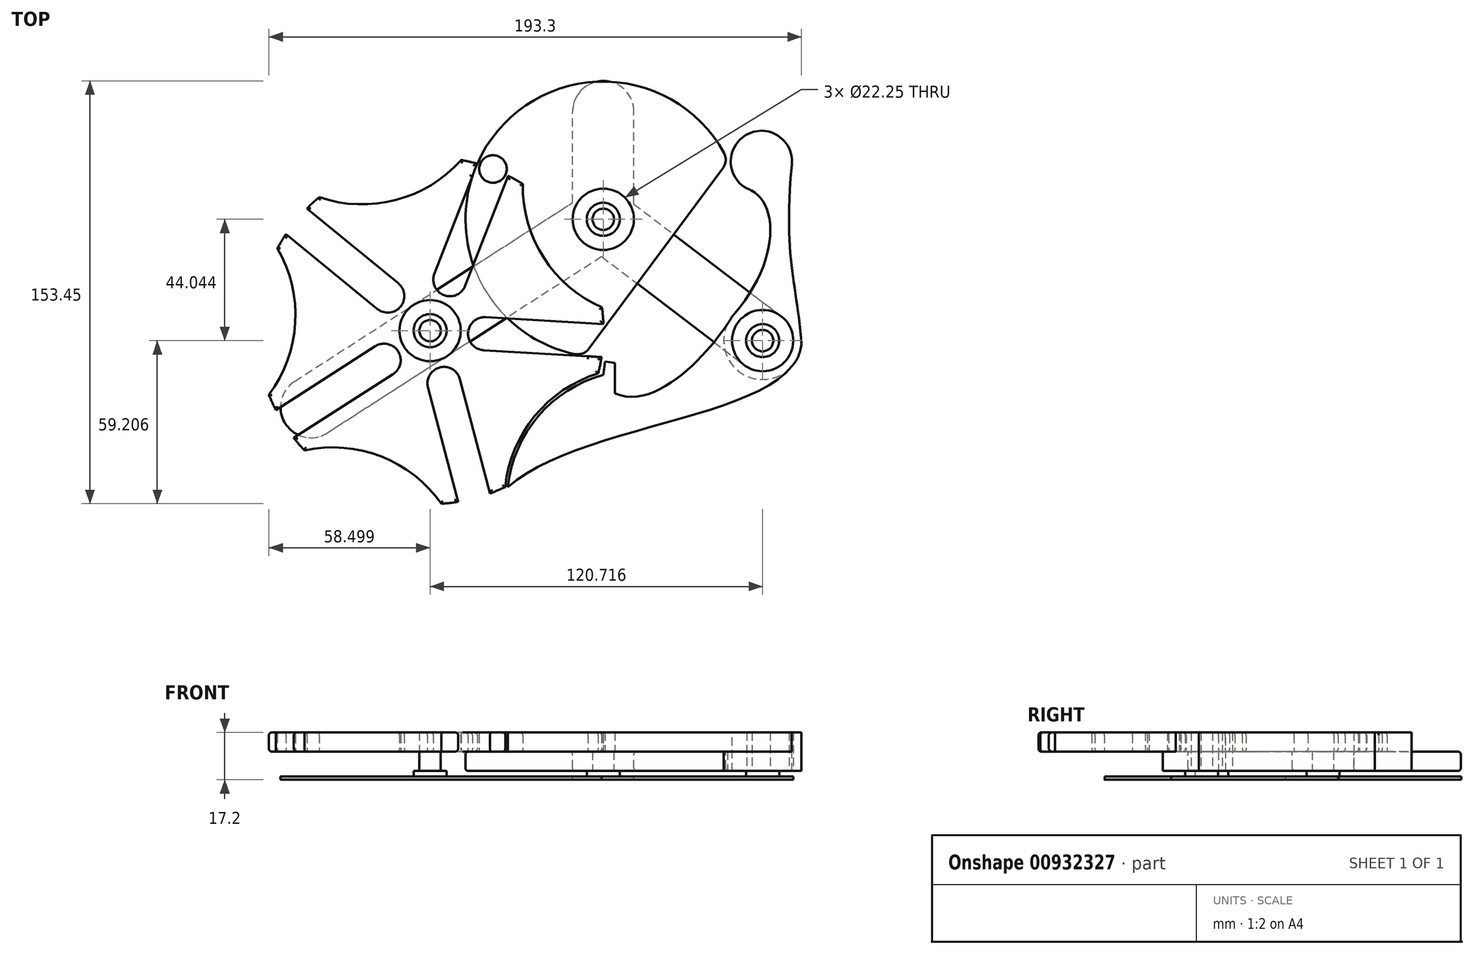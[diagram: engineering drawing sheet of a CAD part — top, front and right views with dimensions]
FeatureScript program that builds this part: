
annotation { "Feature Type Name" : "Feature", "Feature Type Description" : "" }
export const myFeature = defineFeature(function(context is Context, id is Id, definition is map)
    precondition{}
    {
        {
            assignVariable(context, id + "F0", {"name" : "BHeight", "anyValue" : 7});
        }
        {
            var Q0;
            Q0=qCreatedBy(makeId("Top.planeOp"),FACE);
            var sketch = newSketch(context, id + "F1", { "sketchPlane" : qUnion([Q0])});
            skCircle(sketch, "E0", {"center": v(0, 0) * mm, "radius": 11.12 * mm});
            skCircle(sketch, "E1", {"center": v(0, 0) * mm, "radius": 50 * mm});
            skCircle(sketch, "E2", {"center": v(-40.03, 18.26) * mm, "radius": 5 * mm});
            skLineSegment(sketch, "E3", {"start": v(0, 0) * mm, "end": v(-45.5, 20.75) * mm, "construction": true});
            skArc(sketch, "E4", {"start": v(-115.19, -5.4) * mm, "mid": v(-116.8, -7.94) * mm, "end": v(-118.28, -10.55) * mm});
            skLineSegment(sketch, "E5", {"start": v(-40.03, 18.26) * mm, "end": v(-62.86, -40.42) * mm, "construction": true});
            skLineSegment(sketch, "E6", {"start": v(-62.86, -40.42) * mm, "end": v(0, -44) * mm, "construction": true});
            skLineSegment(sketch, "E7", {"start": v(0, 0) * mm, "end": v(0, -44) * mm, "construction": true});
            skLineSegment(sketch, "E8", {"start": v(-34.55, 15.81) * mm, "end": v(-50.08, -24.13) * mm});
            skLineSegment(sketch, "E9", {"start": v(-45.73, 20.16) * mm, "end": v(-61.27, -19.78) * mm});
            skArc(sketch, "E10", {"start": v(-61.27, -19.78) * mm, "mid": v(-57.85, -27.55) * mm, "end": v(-50.08, -24.13) * mm});
            skLineSegment(sketch, "E11.1.0", {"start": v(-115.19, -5.4) * mm, "end": v(-82, -32.53) * mm});
            skLineSegment(sketch, "E11.1.1", {"start": v(-107.6, 3.88) * mm, "end": v(-74.4, -23.24) * mm});
            skArc(sketch, "E11.1.2", {"start": v(-82, -32.53) * mm, "mid": v(-73.56, -31.68) * mm, "end": v(-74.4, -23.24) * mm});
            skLineSegment(sketch, "E11.2.0", {"start": v(-112.33, -79.37) * mm, "end": v(-76.28, -56.19) * mm});
            skLineSegment(sketch, "E11.2.1", {"start": v(-118.82, -69.28) * mm, "end": v(-82.77, -46.1) * mm});
            skArc(sketch, "E11.2.2", {"start": v(-76.28, -56.19) * mm, "mid": v(-74.48, -47.9) * mm, "end": v(-82.77, -46.1) * mm});
            skLineSegment(sketch, "E11.3.0", {"start": v(-41.1, -99.5) * mm, "end": v(-52.02, -58.06) * mm});
            skLineSegment(sketch, "E11.3.1", {"start": v(-52.71, -102.56) * mm, "end": v(-63.62, -61.12) * mm});
            skArc(sketch, "E11.3.2", {"start": v(-52.02, -58.06) * mm, "mid": v(-59.34, -53.79) * mm, "end": v(-63.62, -61.12) * mm});
            skLineSegment(sketch, "E11.4.0", {"start": v(0.05, -38) * mm, "end": v(-42.73, -35.56) * mm});
            skLineSegment(sketch, "E11.4.1", {"start": v(-0.63, -49.97) * mm, "end": v(-43.42, -47.54) * mm});
            skArc(sketch, "E11.4.2", {"start": v(-42.73, -35.56) * mm, "mid": v(-49.07, -41.2) * mm, "end": v(-43.42, -47.54) * mm});
            skCircle(sketch, "E12", {"center": v(-62.86, -40.42) * mm, "radius": 11.12 * mm});
            skArc(sketch, "E13.trimOffspring", {"start": v(-112.33, -79.37) * mm, "mid": v(-110.42, -81.68) * mm, "end": v(-108.4, -83.9) * mm});
            skArc(sketch, "E14.trimOffspring", {"start": v(-41.1, -99.5) * mm, "mid": v(-38.32, -98.4) * mm, "end": v(-35.58, -97.17) * mm});
            skArc(sketch, "E15.trimOffspring", {"start": v(0.05, -38) * mm, "mid": v(-0.13, -35) * mm, "end": v(-0.46, -32.02) * mm});
            skArc(sketch, "E16.trimOffspring", {"start": v(-45.73, 20.16) * mm, "mid": v(-48.64, 20.91) * mm, "end": v(-51.57, 21.52) * mm});
            skArc(sketch, "E17", {"start": v(-1.85, -55.97) * mm, "mid": v(-24.93, -71.48) * mm, "end": v(-35.58, -97.17) * mm});
            skArc(sketch, "E18.trimOffspring", {"start": v(-1.85, -55.97) * mm, "mid": v(-1.16, -52.99) * mm, "end": v(-0.63, -49.97) * mm});
            skArc(sketch, "E19.1.0", {"start": v(-29.22, 12.8) * mm, "mid": v(-21.6, -13.95) * mm, "end": v(-0.46, -32.02) * mm});
            skArc(sketch, "E19.2.0", {"start": v(-103.08, 8.02) * mm, "mid": v(-75.29, 7) * mm, "end": v(-51.57, 21.52) * mm});
            skArc(sketch, "E19.3.0", {"start": v(-121.36, -63.7) * mm, "mid": v(-111.8, -37.6) * mm, "end": v(-118.28, -10.55) * mm});
            skArc(sketch, "E19.4.0", {"start": v(-58.8, -103.25) * mm, "mid": v(-80.68, -86.1) * mm, "end": v(-108.4, -83.9) * mm});
            skCircle(sketch, "E20", {"center": v(57.86, -44.04) * mm, "radius": 11.12 * mm});
            skArc(sketch, "E21.0", {"start": v(0, -56.48) * mm, "mid": v(-23.64, -71.5) * mm, "end": v(-34.59, -97.27) * mm});
            skLineSegment(sketch, "E22", {"start": v(0.7, -51.66) * mm, "end": v(0, -56.48) * mm});
            skLineSegment(sketch, "E23", {"start": v(0.7, -51.66) * mm, "end": v(4.2, -52.16) * mm});
            skLineSegment(sketch, "E24", {"start": v(4.2, -52.16) * mm, "end": v(4.2, -63.16) * mm});
            skCircle(sketch, "E25", {"center": v(57.86, -44.04) * mm, "radius": 14.12 * mm});
            skFitSpline(sketch, "E26", {"points": [v(4.2, -63.16) * mm, v(46.79, -35.27) * mm], "startDerivative": vector(48.84, -21.94) * mm, "endDerivative": vector(16.55, 28.74) * mm});
            skFitSpline(sketch, "E27", {"points": [v(-34.59, -97.27) * mm, v(68.4, -53.43) * mm], "startDerivative": vector(68.8, 63.46) * mm, "endDerivative": vector(45.76, 58.07) * mm});
            skCircle(sketch, "E28", {"center": v(57.4, 21) * mm, "radius": 11.12 * mm});
            skLineSegment(sketch, "E29", {"start": v(28.74, 67) * mm, "end": v(58.91, -15.5) * mm, "construction": true});
            skLineSegment(sketch, "E30", {"start": v(57.4, 21) * mm, "end": v(0, 0) * mm, "construction": true});
            skFitSpline(sketch, "E31", {"points": [v(46.79, -35.27) * mm, v(52.14, 11.2) * mm], "startDerivative": vector(52.8, 59.6) * mm, "endDerivative": vector(-35.98, 12.72) * mm});
            skFitSpline(sketch, "E32", {"points": [v(68.3, 18.76) * mm, v(71.94, -45.11) * mm], "startDerivative": vector(-8.34, -102.87) * mm, "endDerivative": vector(5.33, -69.33) * mm});
            skLineSegment(sketch, "E33", {"start": v(45.32, 21.13) * mm, "end": v(-7.1, -49.5) * mm});
            skLineSegment(sketch, "E34", {"start": v(0, 0) * mm, "end": v(45.32, 21.13) * mm, "construction": true});
            skLineSegment(sketch, "E35", {"start": v(0, 0) * mm, "end": v(-7.1, -49.5) * mm, "construction": true});
            skLineSegment(sketch, "E36", {"start": v(3.77, -49.86) * mm, "end": v(-43.8, 24.11) * mm, "construction": true});
            skArc(sketch, "E37.trimOffspring", {"start": v(-58.8, -103.25) * mm, "mid": v(-55.75, -102.98) * mm, "end": v(-52.71, -102.56) * mm});
            skArc(sketch, "E38.trimOffspring", {"start": v(-121.36, -63.7) * mm, "mid": v(-120.16, -66.52) * mm, "end": v(-118.82, -69.28) * mm});
            skArc(sketch, "E39.trimOffspring", {"start": v(-103.08, 8.02) * mm, "mid": v(-105.39, 6) * mm, "end": v(-107.6, 3.88) * mm});
            skArc(sketch, "E40.trimOffspring", {"start": v(-29.22, 12.8) * mm, "mid": v(-31.85, 14.37) * mm, "end": v(-34.55, 15.81) * mm});
            skSolve(sketch);
        }
        {
            var Q0;
            {var subQ5=sQuery(id+"F1.wireOp",EDGE,"E15.trimOffspring");Q0=makeQuery(id+"F1.imprint","IMPRINT",FACE,{"disambiguationData":[TD([[makeQuery(id+"F1.imprint","IMPRINT",EDGE,{"derivedFrom":subQ5}),1.0]])]});}
            var Q1;
            {var subQ18=sQuery(id+"F1.wireOp",EDGE,"E10");Q1=makeQuery(id+"F1.imprint","IMPRINT",FACE,{"disambiguationData":[TD([[makeQuery(id+"F1.imprint","IMPRINT",EDGE,{"derivedFrom":subQ18}),-1.0]])]});}
            extrude(context, id + "F2", {"entities" : qUnion([Q0, Q1]), "depth" : (getVariable(context, 'BHeight')) * mm, "offsetDistance" : 25 * mm});
        }
        {
            var Q0;
            Q0=makeQuery(id+"F1.imprint","IMPRINT",FACE,{"disambiguationData":[TD([[makeQuery(id+"F1.imprint","IMPRINT",EDGE,{"derivedFrom":sQuery(id+"F1.wireOp",EDGE,"E0")}),-1.0]])]});
            var Q1;
            {var subQ5=sQuery(id+"F1.wireOp",EDGE,"E15.trimOffspring");Q1=makeQuery(id+"F1.imprint","IMPRINT",FACE,{"disambiguationData":[TD([[makeQuery(id+"F1.imprint","IMPRINT",EDGE,{"derivedFrom":subQ5}),1.0]])]});}
            var Q2;
            Q2=makeQuery(id+"F1.imprint","IMPRINT",FACE,{"disambiguationData":[TD([[makeQuery(id+"F1.imprint","IMPRINT",EDGE,{"derivedFrom":sQuery(id+"F1.wireOp",EDGE,"E2")}),1.0]])]});
            var Q3;
            {var subQ0=sQuery(id+"F1.wireOp",EDGE,"E19.1.0");Q3=makeQuery(id+"F1.imprint","IMPRINT",FACE,{"disambiguationData":[TD([[makeQuery(id+"F1.imprint","IMPRINT",EDGE,{"derivedFrom":subQ0}),1.0]])]});}
            var Q4;
            {var subQ0=sQuery(id+"F1.wireOp",EDGE,"E16.trimOffspring");var subQ1=sQuery(id+"F1.wireOp",EDGE,"E1");var subQ2=makeQuery(id+"F1.imprint","INTERSECT",VERTEX,{"derivedFrom":[subQ1,subQ0]});Q4=makeQuery(id+"F1.imprint","IMPRINT",FACE,{"disambiguationData":[TD([[makeQuery(id+"F1.imprint","IMPRINT",EDGE,{"disambiguationData":[TD([[subQ2,-1.0]])],"derivedFrom":subQ1}),1.0]])]});}
            extrude(context, id + "F3", {"entities" : qUnion([Q0, Q1, Q2, Q3, Q4]), "oppositeDirection" : true, "depth" : (getVariable(context, 'BHeight')) * mm, "offsetDistance" : 25 * mm});
        }
        {
            var Q0;
            Q0=makeQuery(id+"F1.imprint","IMPRINT",FACE,{"disambiguationData":[TD([[makeQuery(id+"F1.imprint","IMPRINT",EDGE,{"derivedFrom":sQuery(id+"F1.wireOp",EDGE,"E2")}),1.0]])]});
            var Q1;
            Q1=makeQuery(id+"F2.opExtrude","CAP_FACE",FACE,{"disambiguationData":[OSD([sQuery(id+"F1.wireOp",EDGE,"E1"),sQuery(id+"F1.wireOp",EDGE,"E4"),sQuery(id+"F1.wireOp",EDGE,"E8"),sQuery(id+"F1.wireOp",EDGE,"E9"),sQuery(id+"F1.wireOp",EDGE,"E10"),sQuery(id+"F1.wireOp",EDGE,"E11.1.0"),sQuery(id+"F1.wireOp",EDGE,"E11.1.1"),sQuery(id+"F1.wireOp",EDGE,"E11.1.2"),sQuery(id+"F1.wireOp",EDGE,"E11.2.0"),sQuery(id+"F1.wireOp",EDGE,"E11.2.1"),sQuery(id+"F1.wireOp",EDGE,"E11.2.2"),sQuery(id+"F1.wireOp",EDGE,"E11.3.0"),sQuery(id+"F1.wireOp",EDGE,"E11.3.1"),sQuery(id+"F1.wireOp",EDGE,"E11.3.2"),sQuery(id+"F1.wireOp",EDGE,"E11.4.0"),sQuery(id+"F1.wireOp",EDGE,"E11.4.1"),sQuery(id+"F1.wireOp",EDGE,"E11.4.2"),sQuery(id+"F1.wireOp",EDGE,"E12"),sQuery(id+"F1.wireOp",EDGE,"E13.trimOffspring"),sQuery(id+"F1.wireOp",EDGE,"E14.trimOffspring"),sQuery(id+"F1.wireOp",EDGE,"E15.trimOffspring"),sQuery(id+"F1.wireOp",EDGE,"E16.trimOffspring")])],"isStart":false});
            extrude(context, id + "F4", {"entities" : qUnion([Q0]), "operationType" : NewBodyOperationType.ADD, "endBound" : BoundingType.UP_TO_SURFACE, "depth" : 25 * mm, "endBoundEntityFace" : qUnion([Q1]), "offsetDistance" : 25 * mm});
        }
        {
            var Q0;
            Q0=makeQuery(id+"F3.opExtrude","CAP_FACE",FACE,{"disambiguationData":[OSD([sQuery(id+"F1.wireOp",EDGE,"E0"),sQuery(id+"F1.wireOp",EDGE,"E1"),sQuery(id+"F1.wireOp",EDGE,"E9"),sQuery(id+"F1.wireOp",EDGE,"E11.4.1"),sQuery(id+"F1.wireOp",EDGE,"E14.trimOffspring"),sQuery(id+"F1.wireOp",EDGE,"E16.trimOffspring")])],"isStart":false});
            cPlane(context, id + "F5", {"entities" : qUnion([Q0]), "cplaneType" : CPlaneType.OFFSET, "offset" : 2 * mm, "width" : 150 * mm, "height" : 150 * mm});
        }
        {
            var Q0;
            Q0=makeQuery(id+"F1.imprint","IMPRINT",FACE,{"disambiguationData":[TD([[makeQuery(id+"F1.imprint","IMPRINT",EDGE,{"derivedFrom":sQuery(id+"F1.wireOp",EDGE,"E21.0")}),1.0]])]});
            var Q1;
            Q1=makeQuery(id+"F1.imprint","IMPRINT",FACE,{"disambiguationData":[TD([[makeQuery(id+"F1.imprint","IMPRINT",EDGE,{"derivedFrom":sQuery(id+"F1.wireOp",EDGE,"E20")}),-1.0]])]});
            var Q2;
            Q2=makeQuery(id+"F2.opExtrude","CAP_FACE",FACE,{"disambiguationData":[OSD([sQuery(id+"F1.wireOp",EDGE,"E1"),sQuery(id+"F1.wireOp",EDGE,"E4"),sQuery(id+"F1.wireOp",EDGE,"E8"),sQuery(id+"F1.wireOp",EDGE,"E9"),sQuery(id+"F1.wireOp",EDGE,"E10"),sQuery(id+"F1.wireOp",EDGE,"E11.1.0"),sQuery(id+"F1.wireOp",EDGE,"E11.1.1"),sQuery(id+"F1.wireOp",EDGE,"E11.1.2"),sQuery(id+"F1.wireOp",EDGE,"E11.2.0"),sQuery(id+"F1.wireOp",EDGE,"E11.2.1"),sQuery(id+"F1.wireOp",EDGE,"E11.2.2"),sQuery(id+"F1.wireOp",EDGE,"E11.3.0"),sQuery(id+"F1.wireOp",EDGE,"E11.3.1"),sQuery(id+"F1.wireOp",EDGE,"E11.3.2"),sQuery(id+"F1.wireOp",EDGE,"E11.4.0"),sQuery(id+"F1.wireOp",EDGE,"E11.4.1"),sQuery(id+"F1.wireOp",EDGE,"E11.4.2"),sQuery(id+"F1.wireOp",EDGE,"E12"),sQuery(id+"F1.wireOp",EDGE,"E13.trimOffspring"),sQuery(id+"F1.wireOp",EDGE,"E14.trimOffspring"),sQuery(id+"F1.wireOp",EDGE,"E15.trimOffspring"),sQuery(id+"F1.wireOp",EDGE,"E16.trimOffspring"),sQuery(id+"F1.wireOp",EDGE,"E17"),sQuery(id+"F1.wireOp",EDGE,"E18.trimOffspring"),sQuery(id+"F1.wireOp",EDGE,"E19.1.0"),sQuery(id+"F1.wireOp",EDGE,"E19.2.0"),sQuery(id+"F1.wireOp",EDGE,"E19.3.0"),sQuery(id+"F1.wireOp",EDGE,"E19.4.0")])],"isStart":false});
            extrude(context, id + "F6", {"entities" : qUnion([Q0, Q1]), "endBound" : BoundingType.UP_TO_SURFACE, "depth" : 25 * mm, "endBoundEntityFace" : qUnion([Q2]), "offsetDistance" : 25 * mm});
        }
        {
            var Q0;
            Q0=makeQuery(id+"F1.imprint","IMPRINT",FACE,{"disambiguationData":[TD([[makeQuery(id+"F1.imprint","IMPRINT",EDGE,{"derivedFrom":sQuery(id+"F1.wireOp",EDGE,"E20")}),-1.0]])]});
            var Q1;
            {var subQ0=sQuery(id+"F1.wireOp",EDGE,"E31");var subQ1=sQuery(id+"F1.wireOp",EDGE,"E25");var subQ2=makeQuery(id+"F1.imprint","INTERSECT",VERTEX,{"derivedFrom":[subQ1,subQ0]});Q1=makeQuery(id+"F1.imprint","IMPRINT",FACE,{"disambiguationData":[TD([[makeQuery(id+"F1.imprint","IMPRINT",EDGE,{"disambiguationData":[TD([[subQ2,1.0]])],"derivedFrom":subQ1}),-1.0]])]});}
            var Q2;
            {var subQ0=sQuery(id+"F1.wireOp",EDGE,"E31");var subQ1=sQuery(id+"F1.wireOp",EDGE,"E28");var subQ2=makeQuery(id+"F1.imprint","INTERSECT",VERTEX,{"disambiguationData":[OD(0.0)],"derivedFrom":[subQ1,subQ0]});Q2=makeQuery(id+"F1.imprint","IMPRINT",FACE,{"disambiguationData":[TD([[makeQuery(id+"F1.imprint","IMPRINT",EDGE,{"disambiguationData":[TD([[subQ2,1.0]])],"derivedFrom":subQ1}),1.0]])]});}
            var Q3;
            Q3=makeQuery(id+"F3.opExtrude","CAP_FACE",FACE,{"disambiguationData":[OSD([sQuery(id+"F1.wireOp",EDGE,"E0"),sQuery(id+"F1.wireOp",EDGE,"E1"),sQuery(id+"F1.wireOp",EDGE,"E9"),sQuery(id+"F1.wireOp",EDGE,"E11.4.1"),sQuery(id+"F1.wireOp",EDGE,"E16.trimOffspring"),sQuery(id+"F1.wireOp",EDGE,"E18.trimOffspring")])],"isStart":false});
            extrude(context, id + "F7", {"entities" : qUnion([Q0, Q1, Q2]), "operationType" : NewBodyOperationType.ADD, "endBound" : BoundingType.UP_TO_SURFACE, "oppositeDirection" : true, "depth" : 7 * mm, "endBoundEntityFace" : qUnion([Q3]), "offsetDistance" : 25 * mm});
        }
        {
            var Q0;
            Q0=makeQuery(id+"F7.opExtrude","CAP_FACE",FACE,{"disambiguationData":[OSD([sQuery(id+"F1.wireOp",EDGE,"E20"),sQuery(id+"F1.wireOp",EDGE,"E25"),sQuery(id+"F1.wireOp",EDGE,"E26"),sQuery(id+"F1.wireOp",EDGE,"E28"),sQuery(id+"F1.wireOp",EDGE,"E31"),sQuery(id+"F1.wireOp",EDGE,"E32")])],"isStart":true});
            var Q1;
            Q1=makeQuery(id+"F6.opExtrude","CAP_FACE",FACE,{"disambiguationData":[OSD([sQuery(id+"F1.wireOp",EDGE,"E20"),sQuery(id+"F1.wireOp",EDGE,"E21.0"),sQuery(id+"F1.wireOp",EDGE,"E22"),sQuery(id+"F1.wireOp",EDGE,"E23"),sQuery(id+"F1.wireOp",EDGE,"E24"),sQuery(id+"F1.wireOp",EDGE,"E25"),sQuery(id+"F1.wireOp",EDGE,"E26"),sQuery(id+"F1.wireOp",EDGE,"E27"),sQuery(id+"F1.wireOp",EDGE,"E31"),sQuery(id+"F1.wireOp",EDGE,"E32")])],"isStart":false});
            extrude(context, id + "F8", {"entities" : qUnion([Q0]), "operationType" : NewBodyOperationType.ADD, "endBound" : BoundingType.UP_TO_SURFACE, "depth" : 25 * mm, "endBoundEntityFace" : qUnion([Q1]), "offsetDistance" : 25 * mm});
        }
        {
            var Q0;
            Q0=qCreatedBy(id+"F5.planeOp",FACE);
            var sketch = newSketch(context, id + "F9", { "sketchPlane" : qUnion([Q0])});
            skCircle(sketch, "E41.0", {"center": v(0, 0) * mm, "radius": 11.12 * mm});
            skCircle(sketch, "E42.0", {"center": v(-62.86, 40.42) * mm, "radius": 11.12 * mm});
            skLineSegment(sketch, "E43", {"start": v(-68.88, 31.07) * mm, "end": v(-6.02, -9.36) * mm});
            skLineSegment(sketch, "E44", {"start": v(6.02, 9.36) * mm, "end": v(-56.84, 49.78) * mm});
            skCircle(sketch, "E45.0", {"center": v(57.86, 44.04) * mm, "radius": 11.12 * mm});
            skLineSegment(sketch, "E46", {"start": v(6.74, -8.85) * mm, "end": v(64.6, 35.2) * mm});
            skLineSegment(sketch, "E47", {"start": v(-6.74, 8.85) * mm, "end": v(51.12, 52.9) * mm});
            skCircle(sketch, "E48", {"center": v(57.86, 44.04) * mm, "radius": 6 * mm});
            skCircle(sketch, "E49", {"center": v(0, 0) * mm, "radius": 6 * mm});
            skCircle(sketch, "E50", {"center": v(-62.86, 40.42) * mm, "radius": 6 * mm});
            skCircle(sketch, "E51", {"center": v(-62.86, 40.42) * mm, "radius": 3.88 * mm});
            skCircle(sketch, "E52", {"center": v(0, 0) * mm, "radius": 3.88 * mm});
            skCircle(sketch, "E53", {"center": v(57.86, 44.04) * mm, "radius": 3.88 * mm});
            skCircle(sketch, "E54", {"center": v(-106.03, 68.18) * mm, "radius": 11.12 * mm});
            skCircle(sketch, "E55", {"center": v(0, -39.08) * mm, "radius": 11.12 * mm});
            skLineSegment(sketch, "E56", {"start": v(-112.04, 58.82) * mm, "end": v(-68.88, 31.07) * mm});
            skLineSegment(sketch, "E57", {"start": v(-56.84, 49.78) * mm, "end": v(-100.01, 77.54) * mm});
            skLineSegment(sketch, "E58", {"start": v(-11.12, 0) * mm, "end": v(-11.12, -39.08) * mm});
            skLineSegment(sketch, "E59", {"start": v(11.12, 0) * mm, "end": v(11.13, -39.08) * mm});
            skSolve(sketch);
        }
        {
            var Q0;
            Q0 = qSketchRegion(id + "F9", true);
            var Q1;
            Q1=makeQuery(id+"F9.imprint","IMPRINT",FACE,{"disambiguationData":[TD([[makeQuery(id+"F9.imprint","IMPRINT",EDGE,{"derivedFrom":sQuery(id+"F9.wireOp",EDGE,"E48")}),1.0]])]});
            var Q2;
            Q2=makeQuery(id+"F9.imprint","IMPRINT",FACE,{"disambiguationData":[TD([[makeQuery(id+"F9.imprint","IMPRINT",EDGE,{"derivedFrom":sQuery(id+"F9.wireOp",EDGE,"E53")}),1.0]])]});
            var Q3;
            Q3=makeQuery(id+"F9.imprint","IMPRINT",FACE,{"disambiguationData":[TD([[makeQuery(id+"F9.imprint","IMPRINT",EDGE,{"derivedFrom":sQuery(id+"F9.wireOp",EDGE,"E49")}),1.0]])]});
            var Q4;
            Q4=makeQuery(id+"F9.imprint","IMPRINT",FACE,{"disambiguationData":[TD([[makeQuery(id+"F9.imprint","IMPRINT",EDGE,{"derivedFrom":sQuery(id+"F9.wireOp",EDGE,"E52")}),1.0]])]});
            var Q5;
            Q5=makeQuery(id+"F9.imprint","IMPRINT",FACE,{"disambiguationData":[TD([[makeQuery(id+"F9.imprint","IMPRINT",EDGE,{"derivedFrom":sQuery(id+"F9.wireOp",EDGE,"E50")}),1.0]])]});
            var Q6;
            Q6=makeQuery(id+"F9.imprint","IMPRINT",FACE,{"disambiguationData":[TD([[makeQuery(id+"F9.imprint","IMPRINT",EDGE,{"derivedFrom":sQuery(id+"F9.wireOp",EDGE,"E51")}),1.0]])]});
            var Q7;
            Q7=makeQuery(id+"F9.imprint","IMPRINT",FACE,{"disambiguationData":[TD([[makeQuery(id+"F9.imprint","IMPRINT",EDGE,{"derivedFrom":sQuery(id+"F9.wireOp",EDGE,"E49")}),-1.0]])]});
            extrude(context, id + "F10", {"entities" : qUnion([Q0, Q1, Q2, Q3, Q4, Q5, Q6, Q7]), "depth" : 1.2 * mm, "offsetDistance" : 25 * mm});
        }
        {
            var Q0;
            Q0=makeQuery(id+"F2.opExtrude","CAP_FACE",FACE,{"disambiguationData":[OSD([sQuery(id+"F1.wireOp",EDGE,"E1"),sQuery(id+"F1.wireOp",EDGE,"E4"),sQuery(id+"F1.wireOp",EDGE,"E8"),sQuery(id+"F1.wireOp",EDGE,"E9"),sQuery(id+"F1.wireOp",EDGE,"E10"),sQuery(id+"F1.wireOp",EDGE,"E11.1.0"),sQuery(id+"F1.wireOp",EDGE,"E11.1.1"),sQuery(id+"F1.wireOp",EDGE,"E11.1.2"),sQuery(id+"F1.wireOp",EDGE,"E11.2.0"),sQuery(id+"F1.wireOp",EDGE,"E11.2.1"),sQuery(id+"F1.wireOp",EDGE,"E11.2.2"),sQuery(id+"F1.wireOp",EDGE,"E11.3.0"),sQuery(id+"F1.wireOp",EDGE,"E11.3.1"),sQuery(id+"F1.wireOp",EDGE,"E11.3.2"),sQuery(id+"F1.wireOp",EDGE,"E11.4.0"),sQuery(id+"F1.wireOp",EDGE,"E11.4.1"),sQuery(id+"F1.wireOp",EDGE,"E11.4.2"),sQuery(id+"F1.wireOp",EDGE,"E12"),sQuery(id+"F1.wireOp",EDGE,"E13.trimOffspring"),sQuery(id+"F1.wireOp",EDGE,"E14.trimOffspring"),sQuery(id+"F1.wireOp",EDGE,"E15.trimOffspring"),sQuery(id+"F1.wireOp",EDGE,"E16.trimOffspring"),sQuery(id+"F1.wireOp",EDGE,"E17"),sQuery(id+"F1.wireOp",EDGE,"E18.trimOffspring"),sQuery(id+"F1.wireOp",EDGE,"E19.1.0"),sQuery(id+"F1.wireOp",EDGE,"E19.2.0"),sQuery(id+"F1.wireOp",EDGE,"E19.3.0"),sQuery(id+"F1.wireOp",EDGE,"E19.4.0")])],"isStart":false});
            var Q1;
            Q1=makeQuery(id+"F2.opExtrude","CAP_FACE",FACE,{"disambiguationData":[OSD([sQuery(id+"F1.wireOp",EDGE,"E1"),sQuery(id+"F1.wireOp",EDGE,"E4"),sQuery(id+"F1.wireOp",EDGE,"E8"),sQuery(id+"F1.wireOp",EDGE,"E9"),sQuery(id+"F1.wireOp",EDGE,"E10"),sQuery(id+"F1.wireOp",EDGE,"E11.1.0"),sQuery(id+"F1.wireOp",EDGE,"E11.1.1"),sQuery(id+"F1.wireOp",EDGE,"E11.1.2"),sQuery(id+"F1.wireOp",EDGE,"E11.2.0"),sQuery(id+"F1.wireOp",EDGE,"E11.2.1"),sQuery(id+"F1.wireOp",EDGE,"E11.2.2"),sQuery(id+"F1.wireOp",EDGE,"E11.3.0"),sQuery(id+"F1.wireOp",EDGE,"E11.3.1"),sQuery(id+"F1.wireOp",EDGE,"E11.3.2"),sQuery(id+"F1.wireOp",EDGE,"E11.4.0"),sQuery(id+"F1.wireOp",EDGE,"E11.4.1"),sQuery(id+"F1.wireOp",EDGE,"E11.4.2"),sQuery(id+"F1.wireOp",EDGE,"E12"),sQuery(id+"F1.wireOp",EDGE,"E13.trimOffspring"),sQuery(id+"F1.wireOp",EDGE,"E14.trimOffspring"),sQuery(id+"F1.wireOp",EDGE,"E15.trimOffspring"),sQuery(id+"F1.wireOp",EDGE,"E16.trimOffspring"),sQuery(id+"F1.wireOp",EDGE,"E17"),sQuery(id+"F1.wireOp",EDGE,"E18.trimOffspring"),sQuery(id+"F1.wireOp",EDGE,"E19.1.0"),sQuery(id+"F1.wireOp",EDGE,"E19.2.0"),sQuery(id+"F1.wireOp",EDGE,"E19.3.0"),sQuery(id+"F1.wireOp",EDGE,"E19.4.0")])],"isStart":true});
            var Q2;
            Q2=makeQuery(id+"F6.opExtrude","CAP_FACE",FACE,{"disambiguationData":[OSD([sQuery(id+"F1.wireOp",EDGE,"E20"),sQuery(id+"F1.wireOp",EDGE,"E21.0"),sQuery(id+"F1.wireOp",EDGE,"E22"),sQuery(id+"F1.wireOp",EDGE,"E23"),sQuery(id+"F1.wireOp",EDGE,"E24"),sQuery(id+"F1.wireOp",EDGE,"E25"),sQuery(id+"F1.wireOp",EDGE,"E26"),sQuery(id+"F1.wireOp",EDGE,"E27"),sQuery(id+"F1.wireOp",EDGE,"E31"),sQuery(id+"F1.wireOp",EDGE,"E32")])],"isStart":false});
            var Q3;
            Q3=makeQuery(id+"F4.opExtrude","CAP_FACE",FACE,{"disambiguationData":[OSD([sQuery(id+"F1.wireOp",EDGE,"E2")])],"isStart":false});
            var Q4;
            Q4=makeQuery(id+"F7.opExtrude","CAP_FACE",FACE,{"disambiguationData":[OSD([sQuery(id+"F1.wireOp",EDGE,"E20"),sQuery(id+"F1.wireOp",EDGE,"E25"),sQuery(id+"F1.wireOp",EDGE,"E26"),sQuery(id+"F1.wireOp",EDGE,"E28"),sQuery(id+"F1.wireOp",EDGE,"E31"),sQuery(id+"F1.wireOp",EDGE,"E32")])],"isStart":true});
            var Q5;
            Q5=makeQuery(id+"F7.opExtrude","CAP_FACE",FACE,{"disambiguationData":[OSD([sQuery(id+"F1.wireOp",EDGE,"E20"),sQuery(id+"F1.wireOp",EDGE,"E25"),sQuery(id+"F1.wireOp",EDGE,"E26"),sQuery(id+"F1.wireOp",EDGE,"E28"),sQuery(id+"F1.wireOp",EDGE,"E31"),sQuery(id+"F1.wireOp",EDGE,"E32")])],"isStart":false});
            var Q6;
            Q6=makeQuery(id+"F6.opExtrude","CAP_FACE",FACE,{"disambiguationData":[OSD([sQuery(id+"F1.wireOp",EDGE,"E20"),sQuery(id+"F1.wireOp",EDGE,"E21.0"),sQuery(id+"F1.wireOp",EDGE,"E22"),sQuery(id+"F1.wireOp",EDGE,"E23"),sQuery(id+"F1.wireOp",EDGE,"E24"),sQuery(id+"F1.wireOp",EDGE,"E25"),sQuery(id+"F1.wireOp",EDGE,"E26"),sQuery(id+"F1.wireOp",EDGE,"E27"),sQuery(id+"F1.wireOp",EDGE,"E31"),sQuery(id+"F1.wireOp",EDGE,"E32")])],"isStart":true});
            var Q7;
            Q7=makeQuery(id+"F3.opExtrude","CAP_EDGE",EDGE,{"disambiguationData":[OSD([sQuery(id+"F1.wireOp",EDGE,"E0")])],"isStart":true});
            var Q8;
            Q8=makeQuery(id+"F3.opExtrude","CAP_EDGE",EDGE,{"disambiguationData":[OSD([sQuery(id+"F1.wireOp",EDGE,"E1")])],"isStart":true});
            var Q9;
            Q9=makeQuery(id+"F3.opExtrude","CAP_EDGE",EDGE,{"disambiguationData":[OSD([sQuery(id+"F1.wireOp",EDGE,"E33")])],"isStart":true});
            var Q10;
            Q10=makeQuery(id+"F3.opExtrude","CAP_FACE",FACE,{"disambiguationData":[OSD([sQuery(id+"F1.wireOp",EDGE,"E0"),sQuery(id+"F1.wireOp",EDGE,"E1"),sQuery(id+"F1.wireOp",EDGE,"E33")])],"isStart":false});
            fillet(context, id + "F11", {"entities" : qUnion([Q0, Q1, Q2, Q3, Q4, Q5, Q6, Q7, Q8, Q9, Q10]), "radius" : 1 * mm, "tangentPropagation" : true, "allowEdgeOverflow" : false});
        }
        {
            var Q0;
            {var subQ0=sQuery(id+"F1.wireOp",EDGE,"E33");var subQ1=sQuery(id+"F1.wireOp",EDGE,"E1");Q0=makeQuery(id+"F3.opExtrude","SWEPT_EDGE",EDGE,{"disambiguationData":[OSD([subQ1,subQ0]),TDD([makeQuery(id+"F1.imprint","INTERSECT",VERTEX,{"disambiguationData":[OD(0.0)],"derivedFrom":[subQ1,subQ0]})])]});}
            var Q1;
            {var subQ0=sQuery(id+"F1.wireOp",EDGE,"E33");var subQ1=sQuery(id+"F1.wireOp",EDGE,"E1");Q1=makeQuery(id+"F3.opExtrude","SWEPT_EDGE",EDGE,{"disambiguationData":[OSD([subQ1,subQ0]),TDD([makeQuery(id+"F1.imprint","INTERSECT",VERTEX,{"disambiguationData":[OD(1.0)],"derivedFrom":[subQ1,subQ0]})])]});}
            fillet(context, id + "F12", {"entities" : qUnion([Q0, Q1]), "radius" : 5 * mm, "tangentPropagation" : true, "allowEdgeOverflow" : false});
        }
        {
            var Q0;
            Q0=makeQuery(id+"F9.imprint","IMPRINT",FACE,{"disambiguationData":[TD([[makeQuery(id+"F9.imprint","IMPRINT",EDGE,{"derivedFrom":sQuery(id+"F9.wireOp",EDGE,"E51")}),1.0]])]});
            var Q1;
            Q1=makeQuery(id+"F9.imprint","IMPRINT",FACE,{"disambiguationData":[TD([[makeQuery(id+"F9.imprint","IMPRINT",EDGE,{"derivedFrom":sQuery(id+"F9.wireOp",EDGE,"E53")}),1.0]])]});
            var Q2;
            Q2=makeQuery(id+"F6.opExtrude","CAP_FACE",FACE,{"disambiguationData":[OSD([sQuery(id+"F1.wireOp",EDGE,"E20"),sQuery(id+"F1.wireOp",EDGE,"E21.0"),sQuery(id+"F1.wireOp",EDGE,"E22"),sQuery(id+"F1.wireOp",EDGE,"E23"),sQuery(id+"F1.wireOp",EDGE,"E24"),sQuery(id+"F1.wireOp",EDGE,"E25"),sQuery(id+"F1.wireOp",EDGE,"E26"),sQuery(id+"F1.wireOp",EDGE,"E27"),sQuery(id+"F1.wireOp",EDGE,"E31"),sQuery(id+"F1.wireOp",EDGE,"E32")])],"isStart":false});
            extrude(context, id + "F13", {"entities" : qUnion([Q0, Q1]), "operationType" : NewBodyOperationType.ADD, "endBound" : BoundingType.UP_TO_SURFACE, "oppositeDirection" : true, "depth" : 25 * mm, "endBoundEntityFace" : qUnion([Q2]), "offsetDistance" : 25 * mm});
        }
        {
            var Q0;
            Q0=makeQuery(id+"F9.imprint","IMPRINT",FACE,{"disambiguationData":[TD([[makeQuery(id+"F9.imprint","IMPRINT",EDGE,{"derivedFrom":sQuery(id+"F9.wireOp",EDGE,"E52")}),1.0]])]});
            var Q1;
            Q1=makeQuery(id+"F3.opExtrude","CAP_FACE",FACE,{"disambiguationData":[OSD([sQuery(id+"F1.wireOp",EDGE,"E0"),sQuery(id+"F1.wireOp",EDGE,"E1"),sQuery(id+"F1.wireOp",EDGE,"E33")])],"isStart":true});
            extrude(context, id + "F14", {"entities" : qUnion([Q0]), "operationType" : NewBodyOperationType.ADD, "endBound" : BoundingType.UP_TO_SURFACE, "oppositeDirection" : true, "depth" : 25 * mm, "endBoundEntityFace" : qUnion([Q1]), "offsetDistance" : 25 * mm});
        }
        {
            var Q0;
            Q0=makeQuery(id+"F9.imprint","IMPRINT",FACE,{"disambiguationData":[TD([[makeQuery(id+"F9.imprint","IMPRINT",EDGE,{"derivedFrom":sQuery(id+"F9.wireOp",EDGE,"E48")}),1.0]])]});
            var Q1;
            Q1=makeQuery(id+"F9.imprint","IMPRINT",FACE,{"disambiguationData":[TD([[makeQuery(id+"F9.imprint","IMPRINT",EDGE,{"derivedFrom":sQuery(id+"F9.wireOp",EDGE,"E49")}),1.0]])]});
            var Q2;
            Q2=makeQuery(id+"F9.imprint","IMPRINT",FACE,{"disambiguationData":[TD([[makeQuery(id+"F9.imprint","IMPRINT",EDGE,{"derivedFrom":sQuery(id+"F9.wireOp",EDGE,"E50")}),1.0]])]});
            extrude(context, id + "F15", {"entities" : qUnion([Q0, Q1, Q2]), "operationType" : NewBodyOperationType.ADD, "oppositeDirection" : true, "depth" : 2 * mm, "offsetDistance" : 25 * mm});
        }
    });
